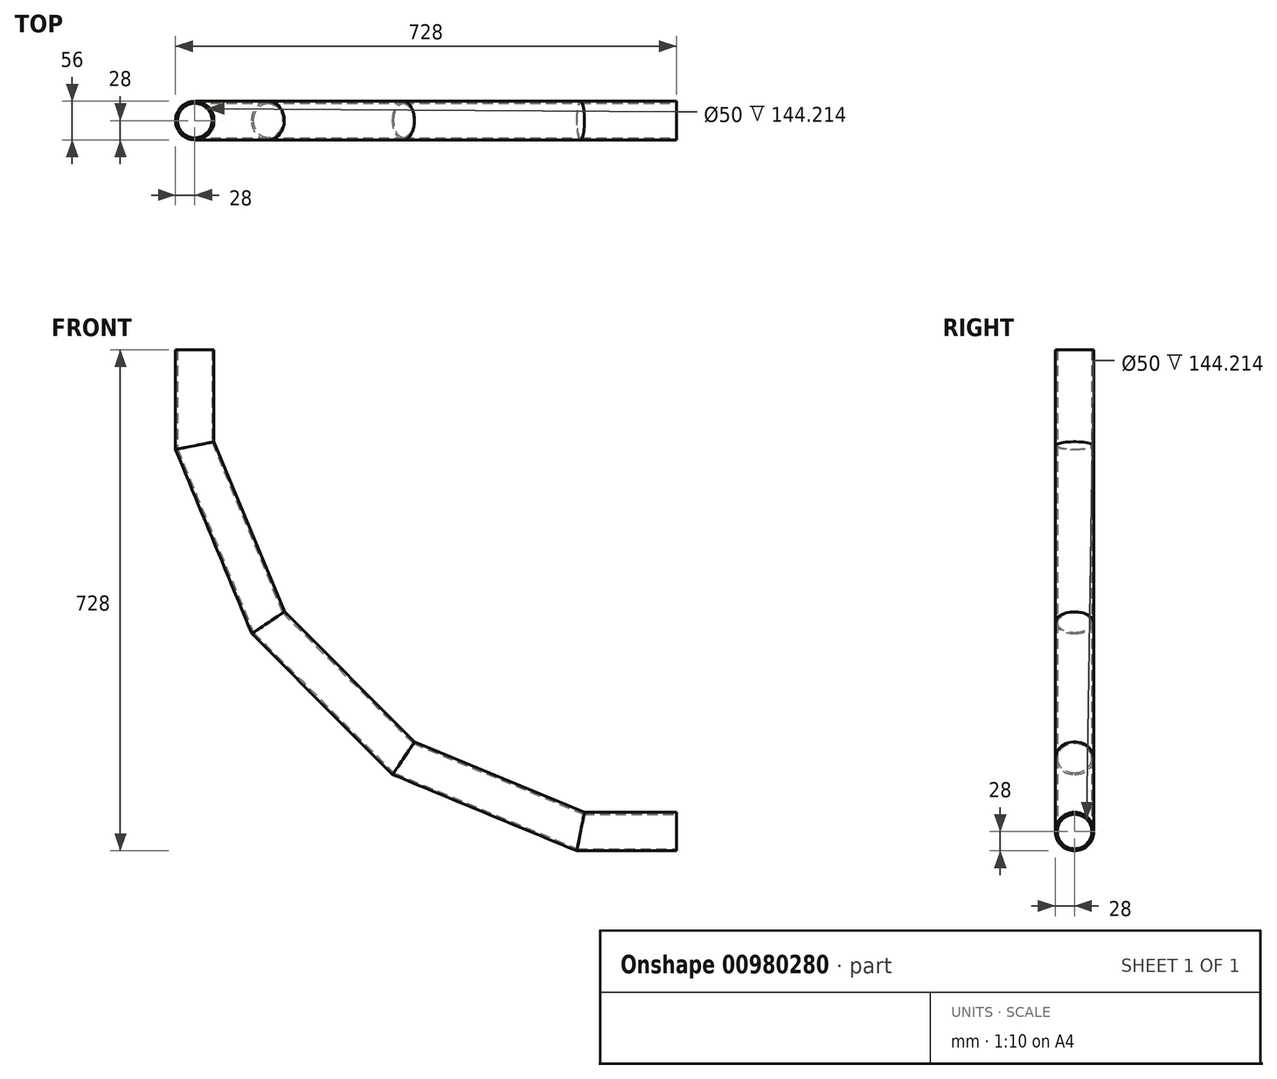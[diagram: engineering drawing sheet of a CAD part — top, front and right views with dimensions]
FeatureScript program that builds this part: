
annotation { "Feature Type Name" : "Feature", "Feature Type Description" : "" }
export const myFeature = defineFeature(function(context is Context, id is Id, definition is map)
    precondition{}
    {
        {
            var Q0;
            Q0=qCreatedBy(makeId("Top.planeOp"),FACE);
            var sketch = newSketch(context, id + "F0", { "sketchPlane" : qUnion([Q0])});
            skCircle(sketch, "E0", {"center": v(0, 0) * mm, "radius": 28 * mm});
            skCircle(sketch, "E1", {"center": v(0, 0) * mm, "radius": 25 * mm});
            skSolve(sketch);
        }
        {
            var Q0;
            Q0=qCreatedBy(makeId("Front.planeOp"),FACE);
            var sketch = newSketch(context, id + "F1", { "sketchPlane" : qUnion([Q0])});
            skLineSegment(sketch, "E2", {"start": v(0, 0) * mm, "end": v(700, 0) * mm, "construction": true});
            skLineSegment(sketch, "E3", {"start": v(700, 0) * mm, "end": v(700, -700) * mm, "construction": true});
            skCircle(sketch, "E4.cCircle", {"center": v(700, 0) * mm, "radius": 700 * mm, "construction": true});
            skLineSegment(sketch, "E4.0", {"start": v(0, -139.24) * mm, "end": v(0, 139.24) * mm, "construction": true});
            skLineSegment(sketch, "E4.1", {"start": v(0, 139.24) * mm, "end": v(106.57, 396.52) * mm, "construction": true});
            skLineSegment(sketch, "E4.2", {"start": v(106.57, 396.52) * mm, "end": v(303.48, 593.43) * mm, "construction": true});
            skLineSegment(sketch, "E4.3", {"start": v(303.48, 593.43) * mm, "end": v(560.76, 700) * mm, "construction": true});
            skLineSegment(sketch, "E4.4", {"start": v(560.76, 700) * mm, "end": v(839.24, 700) * mm, "construction": true});
            skLineSegment(sketch, "E4.5", {"start": v(839.24, 700) * mm, "end": v(1096.52, 593.43) * mm, "construction": true});
            skLineSegment(sketch, "E4.6", {"start": v(1096.52, 593.43) * mm, "end": v(1293.43, 396.52) * mm, "construction": true});
            skLineSegment(sketch, "E4.7", {"start": v(1293.43, 396.52) * mm, "end": v(1400, 139.24) * mm, "construction": true});
            skLineSegment(sketch, "E4.8", {"start": v(1400, 139.24) * mm, "end": v(1400, -139.24) * mm, "construction": true});
            skLineSegment(sketch, "E4.9", {"start": v(1400, -139.24) * mm, "end": v(1293.43, -396.52) * mm, "construction": true});
            skLineSegment(sketch, "E4.10", {"start": v(1293.43, -396.52) * mm, "end": v(1096.52, -593.43) * mm, "construction": true});
            skLineSegment(sketch, "E4.11", {"start": v(1096.52, -593.43) * mm, "end": v(839.24, -700) * mm, "construction": true});
            skLineSegment(sketch, "E4.12", {"start": v(839.24, -700) * mm, "end": v(560.76, -700) * mm, "construction": true});
            skLineSegment(sketch, "E4.13", {"start": v(560.76, -700) * mm, "end": v(303.48, -593.43) * mm});
            skLineSegment(sketch, "E4.14", {"start": v(303.48, -593.43) * mm, "end": v(106.57, -396.52) * mm});
            skLineSegment(sketch, "E4.15", {"start": v(106.57, -396.52) * mm, "end": v(0, -139.24) * mm});
            skPoint(sketch, "E4.0.midPoint", {"position": v(0, 0) * mm});
            skLineSegment(sketch, "E5", {"start": v(0, -139.24) * mm, "end": v(0, 0) * mm});
            skLineSegment(sketch, "E6", {"start": v(560.76, -700) * mm, "end": v(700, -700) * mm});
            skSolve(sketch);
        }
        {
            var Q0;
            Q0 = qSketchRegion(id + "F0", true);
            var Q1;
            Q1 = qConstructionFilter(qBodyType(qCreatedBy(id + "F1" ,EDGE), BodyType.WIRE), ConstructionObject.NO);
            sweep(context, id + "F2", {"profiles" : qUnion([Q0]), "path" : qUnion([Q1])});
        }
    });
